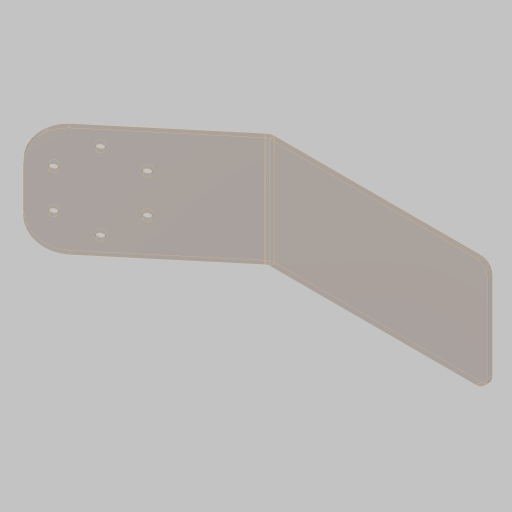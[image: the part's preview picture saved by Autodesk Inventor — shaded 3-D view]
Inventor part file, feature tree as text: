
AUTODESK INVENTOR PART (.ipt)
format: ipt  version: 2023.5 (Build 275446000, 446)  size: 139,776 bytes
history: native  units: in
note: dims shown in document units (in); Inventor stores cm internally (conversion verified against a paired STEP export)
features: sheet_metal_op x4, sketch x3, fillet x2, other x2, hole x1
ambient origin geometry x8: Origin, YZ Plane, XZ Plane, XY Plane, X Axis, Y Axis, Z Axis, Center Point
bodies: Solid1 (feature_tree)
feature tree (12):
  sheet_metal_op  "Face1"
  sheet_metal_op  "Flange1"
  hole  "Hole1"  [1 undecoded]
  fillet  "Fillet1"  Radius=0.12in
  fillet  "Fillet2"  Radius=0.12in
  sketch  "Sketch1"  dims[d0=2.5in d1=5.0in d2=0.12in d3=0.12in]
  other  "Plate1"
  sketch  "Sketch2"  dims[d4=0.06in]
  other  "Plate2"
  sheet_metal_op  "Bend1"
  sheet_metal_op  "Corner1"
  sketch  "Sketch3"  dims[d5=0.24in d6=0.12in d7=4.0in d8=0.2749in d9=0.12in d10=0.48in d11=0.12in d12=0.12in d13=1.75in d14=2.3622in d16=360.0deg d18=0.177in d19=0.75in d20=0.385in d21=0.063in d22=0.5635in d23=0.12in d24=0.8108in d25=1.25in d26=0.75in d27=0.25in]
note: 1 required parameter value undecoded (feature->parameter linkage not recoverable at this tier; creation-order binding heuristic only, values carry confidence <= 0.55)
